# Revit family: Joist_NewMillennium_LH-Series_DblPitch
name_source: partatom
category: Structural Framing
units: mm (PartAtom-declared; Revit-internal decimal feet)

## family parameters
Always export as geometry = No
Always vertical = Yes
Classification Number = 23.25.30.21.14.11
Cut with Voids When Loaded = No
Material for Model Behavior = Steel
Section Shape = Not Defined
Shared = No
Show family pre-cut in plan views = Yes

## types (7) — shared parameters
Assembly Code = B1010350
Bearing Seat = Yes
Building Codes = https://www.newmill.com
Channel Width = 0' - 1 1/8"
Construction Details = https://www.newmill.com
Description = New Millennium Building Systems LH Series - Double Pitch
Green Building-LEED = http://www.arcat.com
Installation-Fabrication = https://www.newmill.com
Keynote = 05 21 00
Lower Chord Representation = Metal - Steel
Manufacturer = New Millennium Building Systems
Manufacturer Fax = 260-868-6002
Manufacturer Website = https://www.newmill.com
Model = LH Series - Double Pitch
Product Data = http://www.arcat.com
Revision = R0_10-2017
Roundover = 0' - 0 1/4"
Sales Information = https://www.newmill.com
Seat Length = 0' - 9"
SeatWdth = 0' - 2 1/8"
Specification = http://www.arcat.com
TXTLoc = 0' - 4"
Test Data = https://www.newmill.com
Thickness_Channel = 0' - 0 3/16"
Thickness_Lower = 0' - 0 1/2"
Thickness_Upper = 0' - 0 1/2"
Type Comments = Contact New Millennium for Structural Web Design
URL = https://www.newmill.com
Upper Chord Representation = Metal - Steel
Web Infill = Metal - Steel

## per-type parameters (varying)
| type | Angle Size_Lower | Angle Size_Upper | Height | Max Length | SeatHalf |
| 18 in Depth / 36 Ft Max Length | 0' - 1 1/2" | 0' - 1 1/2" | 1' - 6" | 36' - 0" | 0' - 2 1/16" |
| 20 in Depth / 40 Ft Max Length | 0' - 1 1/2" | 0' - 1 1/2" | 1' - 8" | 40' - 0" | 0' - 2 1/16" |
| 24 in Depth / 48 Ft Max Length | 0' - 1 1/2" | 0' - 1 3/4" | 2' - 0" | 48' - 0" | 0' - 2 5/16" |
| 28 in Depth / 56 Ft Max Length | 0' - 2" | 0' - 2" | 2' - 4" | 56' - 0" | 0' - 2 9/16" |
| 32 in Depth / 64 Ft Max Length | 0' - 2 1/2" | 0' - 3" | 2' - 8" | 64' - 0" | 0' - 3 9/16" |
| 36 in Depth / 72 Ft Max Length | 0' - 3" | 0' - 3" | 3' - 0" | 72' - 0" | 0' - 3 9/16" |
| 40 in Depth / 80 Ft Max Length | 0' - 3" | 0' - 3 1/2" | 3' - 4" | 80' - 0" | 0' - 4 1/16" |

## geometry (parser evidence)
native form markers: Sweep x3
no freeform markers — native parametric forms only
